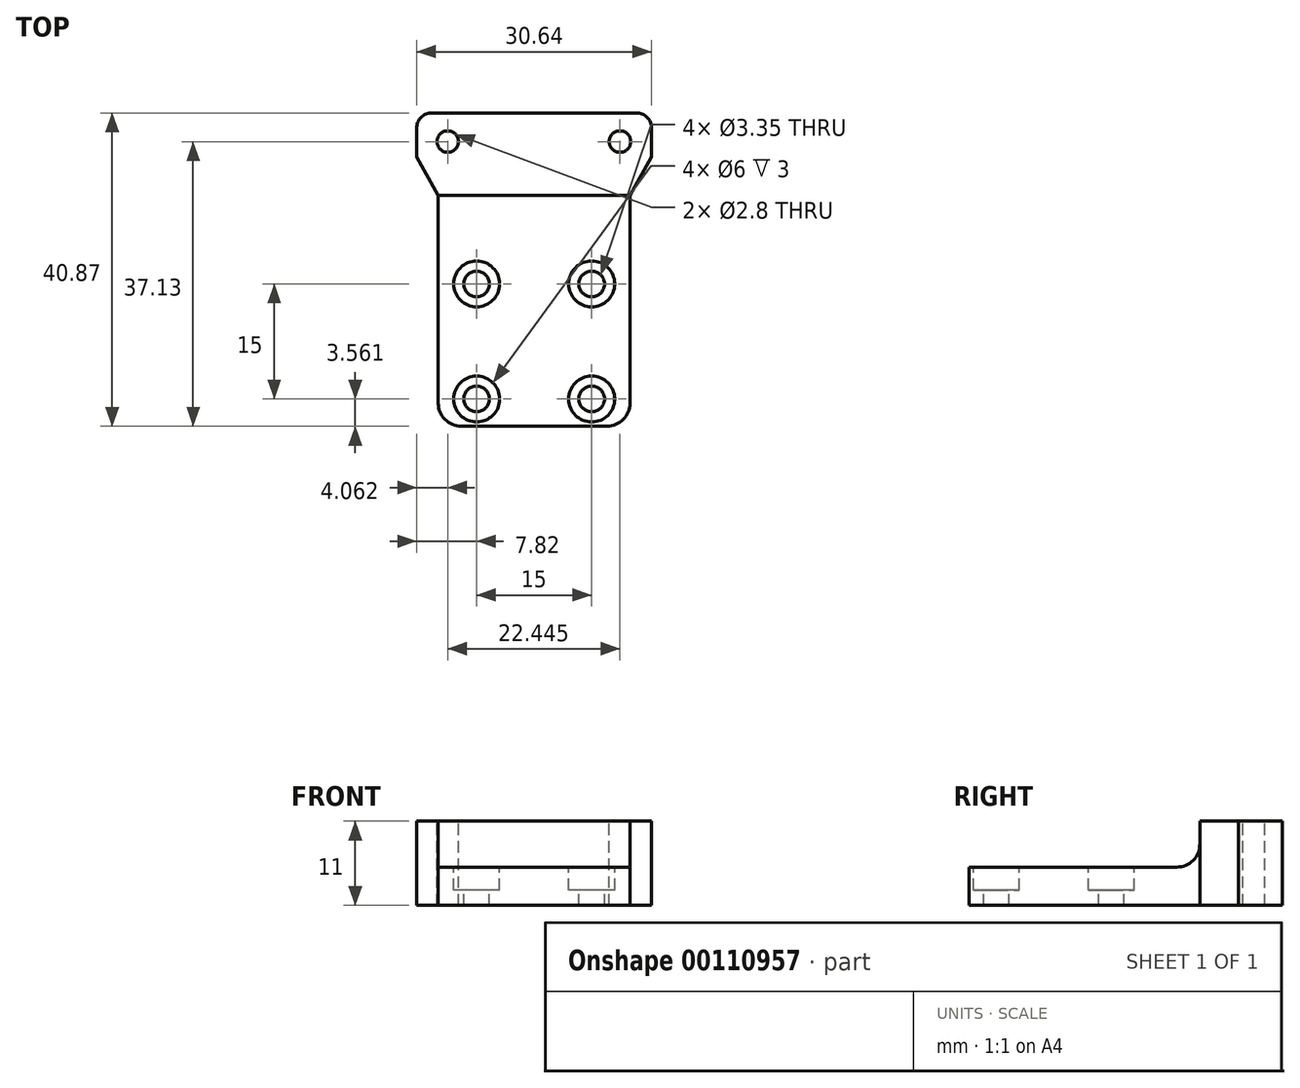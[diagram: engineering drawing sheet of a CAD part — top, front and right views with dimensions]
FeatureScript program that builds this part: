
annotation { "Feature Type Name" : "Feature", "Feature Type Description" : "" }
export const myFeature = defineFeature(function(context is Context, id is Id, definition is map)
    precondition{}
    {
        {
            var Q0;
            Q0=qCreatedBy(makeId("Top.planeOp"),FACE);
            var sketch = newSketch(context, id + "F0", { "sketchPlane" : qUnion([Q0])});
            skLineSegment(sketch, "E0.bottom", {"start": v(0, 0) * mm, "end": v(25, 0) * mm});
            skLineSegment(sketch, "E0.top", {"start": v(-2.82, 40.87) * mm, "end": v(27.82, 40.87) * mm});
            skLineSegment(sketch, "E1", {"start": v(0, 30.1) * mm, "end": v(25, 30.1) * mm});
            skLineSegment(sketch, "E2", {"start": v(-2.82, 35.1) * mm, "end": v(27.82, 35.1) * mm});
            skLineSegment(sketch, "E3", {"start": v(0, 0) * mm, "end": v(0, 30.1) * mm});
            skLineSegment(sketch, "E4", {"start": v(0, 30.1) * mm, "end": v(-2.82, 35.1) * mm});
            skLineSegment(sketch, "E5", {"start": v(-2.82, 35.1) * mm, "end": v(-2.82, 40.87) * mm});
            skLineSegment(sketch, "E6", {"start": v(25, 0) * mm, "end": v(25, 30.1) * mm});
            skLineSegment(sketch, "E7", {"start": v(25, 30.1) * mm, "end": v(27.82, 35.1) * mm});
            skLineSegment(sketch, "E8", {"start": v(27.82, 35.1) * mm, "end": v(27.82, 40.87) * mm});
            skSolve(sketch);
        }
        {
            var Q0;
            Q0=qSketchRegion(id+"F0",true);
            extrude(context, id + "F1", {"entities" : qUnion([Q0]), "depth" : 5 * mm});
        }
        {
            var Q0;
            Q0=makeQuery(id+"F1.opExtrude","CAP_FACE",FACE,{"disambiguationData":[OSD([sQuery(id+"F0.wireOp",EDGE,"E0.bottom"),sQuery(id+"F0.wireOp",EDGE,"E0.top"),sQuery(id+"F0.wireOp",EDGE,"E3"),sQuery(id+"F0.wireOp",EDGE,"E4"),sQuery(id+"F0.wireOp",EDGE,"E5"),sQuery(id+"F0.wireOp",EDGE,"E6"),sQuery(id+"F0.wireOp",EDGE,"E7"),sQuery(id+"F0.wireOp",EDGE,"E8")])],"isStart":false});
            var sketch = newSketch(context, id + "F2", { "sketchPlane" : qUnion([Q0])});
            skCircle(sketch, "E9", {"center": v(5, 18.56) * mm, "radius": 1.68 * mm});
            skCircle(sketch, "E10", {"center": v(20, 18.56) * mm, "radius": 1.68 * mm});
            skCircle(sketch, "E11", {"center": v(5, 3.56) * mm, "radius": 1.68 * mm});
            skCircle(sketch, "E12", {"center": v(20, 3.56) * mm, "radius": 1.68 * mm});
            skLineSegment(sketch, "E13", {"start": v(5, 18.56) * mm, "end": v(0, 18.56) * mm});
            skLineSegment(sketch, "E14", {"start": v(20, 3.56) * mm, "end": v(25, 3.56) * mm});
            skCircle(sketch, "E15", {"center": v(5, 18.56) * mm, "radius": 3 * mm});
            skCircle(sketch, "E16", {"center": v(20, 18.56) * mm, "radius": 3 * mm});
            skCircle(sketch, "E17", {"center": v(5, 3.56) * mm, "radius": 3 * mm});
            skCircle(sketch, "E18", {"center": v(20, 3.56) * mm, "radius": 3 * mm});
            skSolve(sketch);
        }
        {
            var Q0;
            Q0=makeQuery(id+"F2.imprint","IMPRINT",FACE,{"disambiguationData":[TD([[makeQuery(id+"F2.imprint","IMPRINT",EDGE,{"derivedFrom":sQuery(id+"F2.wireOp",EDGE,"E9")}),1.0]])]});
            var Q1;
            Q1=makeQuery(id+"F2.imprint","IMPRINT",FACE,{"disambiguationData":[TD([[makeQuery(id+"F2.imprint","IMPRINT",EDGE,{"derivedFrom":sQuery(id+"F2.wireOp",EDGE,"E10")}),1.0]])]});
            var Q2;
            Q2=makeQuery(id+"F2.imprint","IMPRINT",FACE,{"disambiguationData":[TD([[makeQuery(id+"F2.imprint","IMPRINT",EDGE,{"derivedFrom":sQuery(id+"F2.wireOp",EDGE,"E12")}),1.0]])]});
            var Q3;
            Q3=makeQuery(id+"F2.imprint","IMPRINT",FACE,{"disambiguationData":[TD([[makeQuery(id+"F2.imprint","IMPRINT",EDGE,{"derivedFrom":sQuery(id+"F2.wireOp",EDGE,"E11")}),1.0]])]});
            var Q4;
            Q4=makeQuery(id+"F2.imprint","IMPRINT",FACE,{"disambiguationData":[TD([[makeQuery(id+"F2.imprint","IMPRINT",EDGE,{"derivedFrom":sQuery(id+"F2.wireOp",EDGE,"97d24b09-4827-4c46-a1fd-a3ea8677536d")}),1.0]])]});
            var Q5;
            Q5=makeQuery(id+"F2.imprint","IMPRINT",FACE,{"disambiguationData":[TD([[makeQuery(id+"F2.imprint","IMPRINT",EDGE,{"derivedFrom":sQuery(id+"F2.wireOp",EDGE,"b6eb7b6f-8bb0-4363-9520-a6d7085f5256")}),1.0]])]});
            extrude(context, id + "F3", {"entities" : qUnion([Q0, Q1, Q2, Q3, Q4, Q5]), "operationType" : NewBodyOperationType.REMOVE, "oppositeDirection" : true, "depth" : 25 * mm});
        }
        {
            var Q0;
            Q0=makeQuery(id+"F1.opExtrude","SWEPT_EDGE",EDGE,{"disambiguationData":[OSD([sQuery(id+"F0.wireOp",EDGE,"E0.bottom"),sQuery(id+"F0.wireOp",EDGE,"E0.left")])]});
            var Q1;
            Q1=makeQuery(id+"F1.opExtrude","SWEPT_EDGE",EDGE,{"disambiguationData":[OSD([sQuery(id+"F0.wireOp",EDGE,"E0.bottom"),sQuery(id+"F0.wireOp",EDGE,"E0.right")])]});
            fillet(context, id + "F4", {"entities" : qUnion([Q0, Q1]), "radius" : 3 * mm, "tangentPropagation" : true, "allowEdgeOverflow" : false});
        }
        {
            var Q0;
            Q0=makeQuery(id+"F0.imprint","IMPRINT",FACE,{"disambiguationData":[TD([[makeQuery(id+"F0.imprint","IMPRINT",EDGE,{"derivedFrom":sQuery(id+"F0.wireOp",EDGE,"E0.top")}),-1.0]])]});
            var Q1;
            Q1=makeQuery(id+"F0.imprint","IMPRINT",FACE,{"disambiguationData":[TD([[makeQuery(id+"F0.imprint","IMPRINT",EDGE,{"derivedFrom":sQuery(id+"F0.wireOp",EDGE,"E1")}),1.0]])]});
            extrude(context, id + "F5", {"entities" : qUnion([Q0, Q1]), "operationType" : NewBodyOperationType.ADD, "depth" : 11 * mm});
        }
        {
            var Q0;
            Q0=makeQuery(id+"F5.opExtrude","CAP_FACE",FACE,{"disambiguationData":[OSD([sQuery(id+"F0.wireOp",EDGE,"E0.top"),sQuery(id+"F0.wireOp",EDGE,"E1"),sQuery(id+"F0.wireOp",EDGE,"E4"),sQuery(id+"F0.wireOp",EDGE,"E5"),sQuery(id+"F0.wireOp",EDGE,"E7"),sQuery(id+"F0.wireOp",EDGE,"E8")])],"isStart":false});
            var sketch = newSketch(context, id + "F6", { "sketchPlane" : qUnion([Q0])});
            skCircle(sketch, "E19", {"center": v(23.69, 37.13) * mm, "radius": 1.4 * mm});
            skCircle(sketch, "E20", {"center": v(1.24, 37.13) * mm, "radius": 1.4 * mm});
            skLineSegment(sketch, "E21", {"start": v(1.24, 37.13) * mm, "end": v(-2.82, 37.13) * mm});
            skLineSegment(sketch, "E22", {"start": v(23.69, 37.13) * mm, "end": v(27.75, 37.13) * mm});
            skSolve(sketch);
        }
        {
            var Q0;
            Q0=qSketchRegion(id+"F6",true);
            extrude(context, id + "F7", {"entities" : qUnion([Q0]), "operationType" : NewBodyOperationType.REMOVE, "endBound" : BoundingType.THROUGH_ALL, "oppositeDirection" : true, "depth" : 25 * mm});
        }
        {
            var Q0;
            Q0=makeQuery(id+"F2.imprint","IMPRINT",FACE,{"disambiguationData":[TD([[makeQuery(id+"F2.imprint","IMPRINT",EDGE,{"derivedFrom":sQuery(id+"F2.wireOp",EDGE,"E9")}),-1.0]])]});
            var Q1;
            Q1=makeQuery(id+"F2.imprint","IMPRINT",FACE,{"disambiguationData":[TD([[makeQuery(id+"F2.imprint","IMPRINT",EDGE,{"derivedFrom":sQuery(id+"F2.wireOp",EDGE,"E11")}),-1.0]])]});
            var Q2;
            Q2=makeQuery(id+"F2.imprint","IMPRINT",FACE,{"disambiguationData":[TD([[makeQuery(id+"F2.imprint","IMPRINT",EDGE,{"derivedFrom":sQuery(id+"F2.wireOp",EDGE,"E10")}),-1.0]])]});
            var Q3;
            Q3=makeQuery(id+"F2.imprint","IMPRINT",FACE,{"disambiguationData":[TD([[makeQuery(id+"F2.imprint","IMPRINT",EDGE,{"derivedFrom":sQuery(id+"F2.wireOp",EDGE,"E12")}),-1.0]])]});
            extrude(context, id + "F8", {"entities" : qUnion([Q0, Q1, Q2, Q3]), "operationType" : NewBodyOperationType.REMOVE, "oppositeDirection" : true, "depth" : 3 * mm});
        }
        {
            var Q0;
            Q0=makeQuery(id+"F5.boolean.opBoolean","INTERSECT",EDGE,{"derivedFrom":[makeQuery(id+"F1.opExtrude","CAP_FACE",FACE,{"disambiguationData":[OSD([sQuery(id+"F0.wireOp",EDGE,"E0.bottom"),sQuery(id+"F0.wireOp",EDGE,"E0.top"),sQuery(id+"F0.wireOp",EDGE,"E3"),sQuery(id+"F0.wireOp",EDGE,"E4"),sQuery(id+"F0.wireOp",EDGE,"E5"),sQuery(id+"F0.wireOp",EDGE,"E6"),sQuery(id+"F0.wireOp",EDGE,"E7"),sQuery(id+"F0.wireOp",EDGE,"E8")])],"isStart":false}),makeQuery(id+"F5.opExtrude","SWEPT_FACE",FACE,{"disambiguationData":[OSD([sQuery(id+"F0.wireOp",EDGE,"E1")])]})]});
            fillet(context, id + "F9", {"entities" : qUnion([Q0]), "radius" : 3 * mm, "tangentPropagation" : true, "allowEdgeOverflow" : false});
        }
        {
            var Q0;
            {var subQ0=sQuery(id+"F0.wireOp",EDGE,"E8");var subQ1=sQuery(id+"F0.wireOp",EDGE,"E0.top");Q0=makeQuery(id+"F5.boolean.opBoolean","MERGE",EDGE,{"derivedFrom":[makeQuery(id+"F1.opExtrude","SWEPT_EDGE",EDGE,{"disambiguationData":[OSD([subQ1,subQ0])]}),makeQuery(id+"F5.opExtrude","SWEPT_EDGE",EDGE,{"disambiguationData":[OSD([subQ1,subQ0])]})]});}
            var Q1;
            {var subQ0=sQuery(id+"F0.wireOp",EDGE,"E5");var subQ1=sQuery(id+"F0.wireOp",EDGE,"E0.top");Q1=makeQuery(id+"F5.boolean.opBoolean","MERGE",EDGE,{"derivedFrom":[makeQuery(id+"F1.opExtrude","SWEPT_EDGE",EDGE,{"disambiguationData":[OSD([subQ1,subQ0])]}),makeQuery(id+"F5.opExtrude","SWEPT_EDGE",EDGE,{"disambiguationData":[OSD([subQ1,subQ0])]})]});}
            fillet(context, id + "F10", {"entities" : qUnion([Q0, Q1]), "radius" : 2 * mm, "tangentPropagation" : true, "allowEdgeOverflow" : false});
        }
    });
